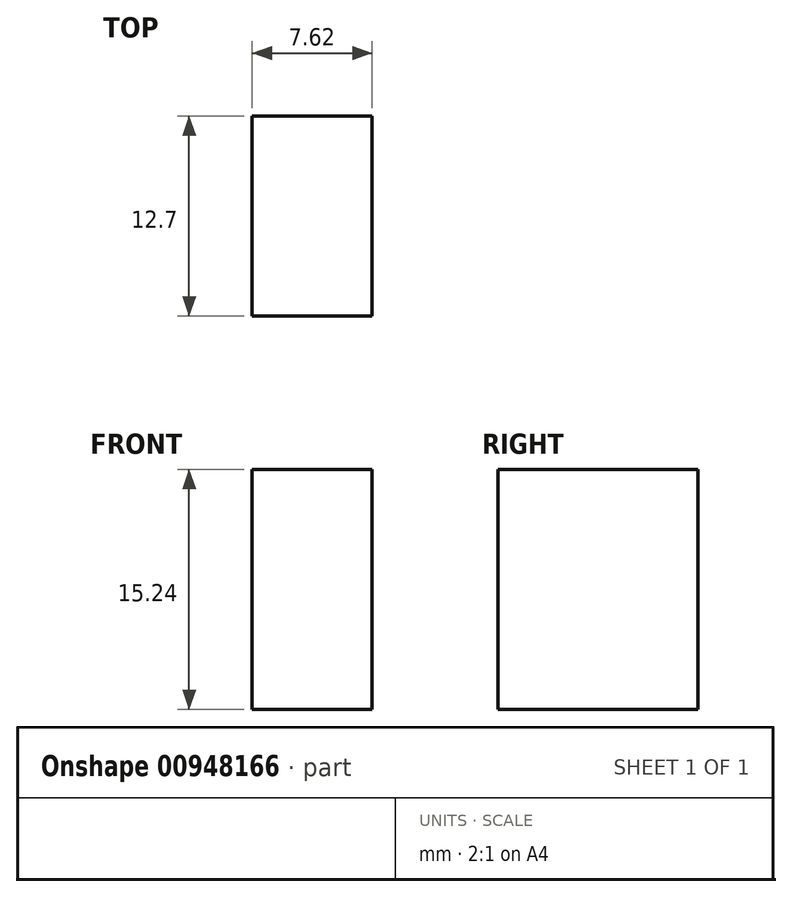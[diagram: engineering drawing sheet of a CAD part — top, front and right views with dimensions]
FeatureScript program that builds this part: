
annotation { "Feature Type Name" : "Feature", "Feature Type Description" : "" }
export const myFeature = defineFeature(function(context is Context, id is Id, definition is map)
    precondition{}
    {
        {
            var Q0;
            Q0=qCreatedBy(makeId("Right.planeOp"),FACE);
            var sketch = newSketch(context, id + "F0", { "sketchPlane" : qUnion([Q0])});
            skLineSegment(sketch, "E0.bottom", {"start": v(-47.08, 45.25) * mm, "end": v(-34.38, 45.25) * mm});
            skLineSegment(sketch, "E0.top", {"start": v(-47.08, 30.01) * mm, "end": v(-34.38, 30.01) * mm});
            skLineSegment(sketch, "E0.left", {"start": v(-47.08, 45.25) * mm, "end": v(-47.08, 30.01) * mm});
            skLineSegment(sketch, "E0.right", {"start": v(-34.38, 45.25) * mm, "end": v(-34.38, 30.01) * mm});
            skSolve(sketch);
        }
        {
            var Q0;
            Q0=makeQuery(id+"F0.imprint","IMPRINT",FACE,{"disambiguationData":[TD([[makeQuery(id+"F0.imprint","IMPRINT",EDGE,{"derivedFrom":sQuery(id+"F0.wireOp",EDGE,"E0.bottom")}),-1.0]])]});
            extrude(context, id + "F1", {"entities" : qUnion([Q0]), "oppositeDirection" : true, "depth" : 7.62 * mm, "offsetDistance" : 25.4 * mm});
        }
    });
